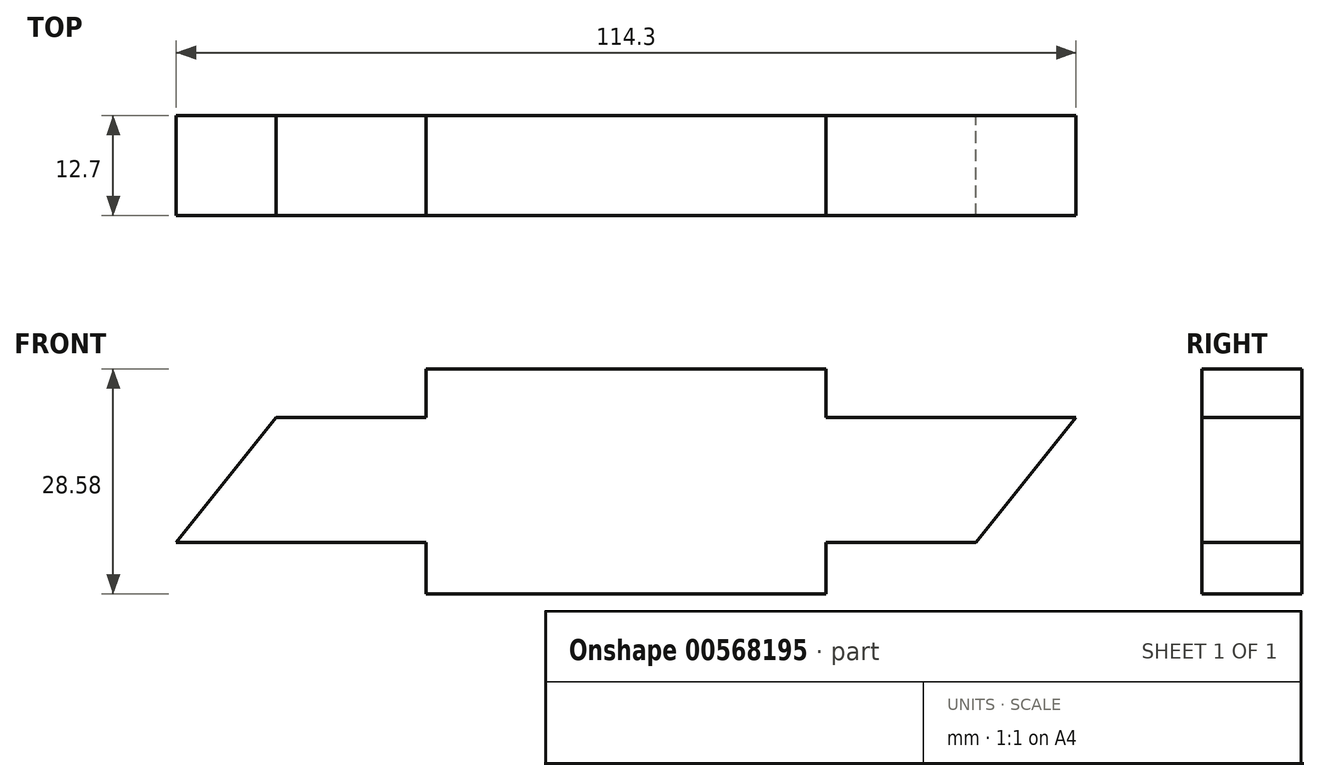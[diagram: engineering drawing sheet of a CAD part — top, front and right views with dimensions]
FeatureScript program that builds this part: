
annotation { "Feature Type Name" : "Feature", "Feature Type Description" : "" }
export const myFeature = defineFeature(function(context is Context, id is Id, definition is map)
    precondition{}
    {
        {
            var Q0;
            Q0=qCreatedBy(makeId("Front.planeOp"),FACE);
            var sketch = newSketch(context, id + "F0", { "sketchPlane" : qUnion([Q0])});
            skLineSegment(sketch, "E0.bottom", {"start": v(-25.4, 14.29) * mm, "end": v(25.4, 14.29) * mm});
            skLineSegment(sketch, "E0.top", {"start": v(-25.4, -14.29) * mm, "end": v(25.4, -14.29) * mm});
            skLineSegment(sketch, "E0.left", {"start": v(-25.4, 14.29) * mm, "end": v(-25.4, -14.29) * mm});
            skLineSegment(sketch, "E0.right", {"start": v(25.4, 14.29) * mm, "end": v(25.4, -14.29) * mm});
            skPoint(sketch, "E0.middle", {"position": v(0, 0) * mm});
            skLineSegment(sketch, "E1", {"start": v(-25.4, -7.76) * mm, "end": v(-57.15, -7.76) * mm});
            skLineSegment(sketch, "E2", {"start": v(-25.4, 8.1) * mm, "end": v(-44.45, 8.1) * mm});
            skLineSegment(sketch, "E3", {"start": v(-57.15, -7.76) * mm, "end": v(-44.45, 8.1) * mm});
            skLineSegment(sketch, "E4", {"start": v(25.4, 8.1) * mm, "end": v(57.15, 8.1) * mm});
            skLineSegment(sketch, "E5", {"start": v(25.4, -7.76) * mm, "end": v(44.45, -7.76) * mm});
            skLineSegment(sketch, "E6", {"start": v(57.15, 8.1) * mm, "end": v(44.45, -7.76) * mm});
            skSolve(sketch);
        }
        {
            var Q0;
            Q0 = qSketchRegion(id + "F0", true);
            extrude(context, id + "F1", {"entities" : qUnion([Q0]), "depth" : 12.7 * mm, "offsetDistance" : 25.4 * mm});
        }
    });
